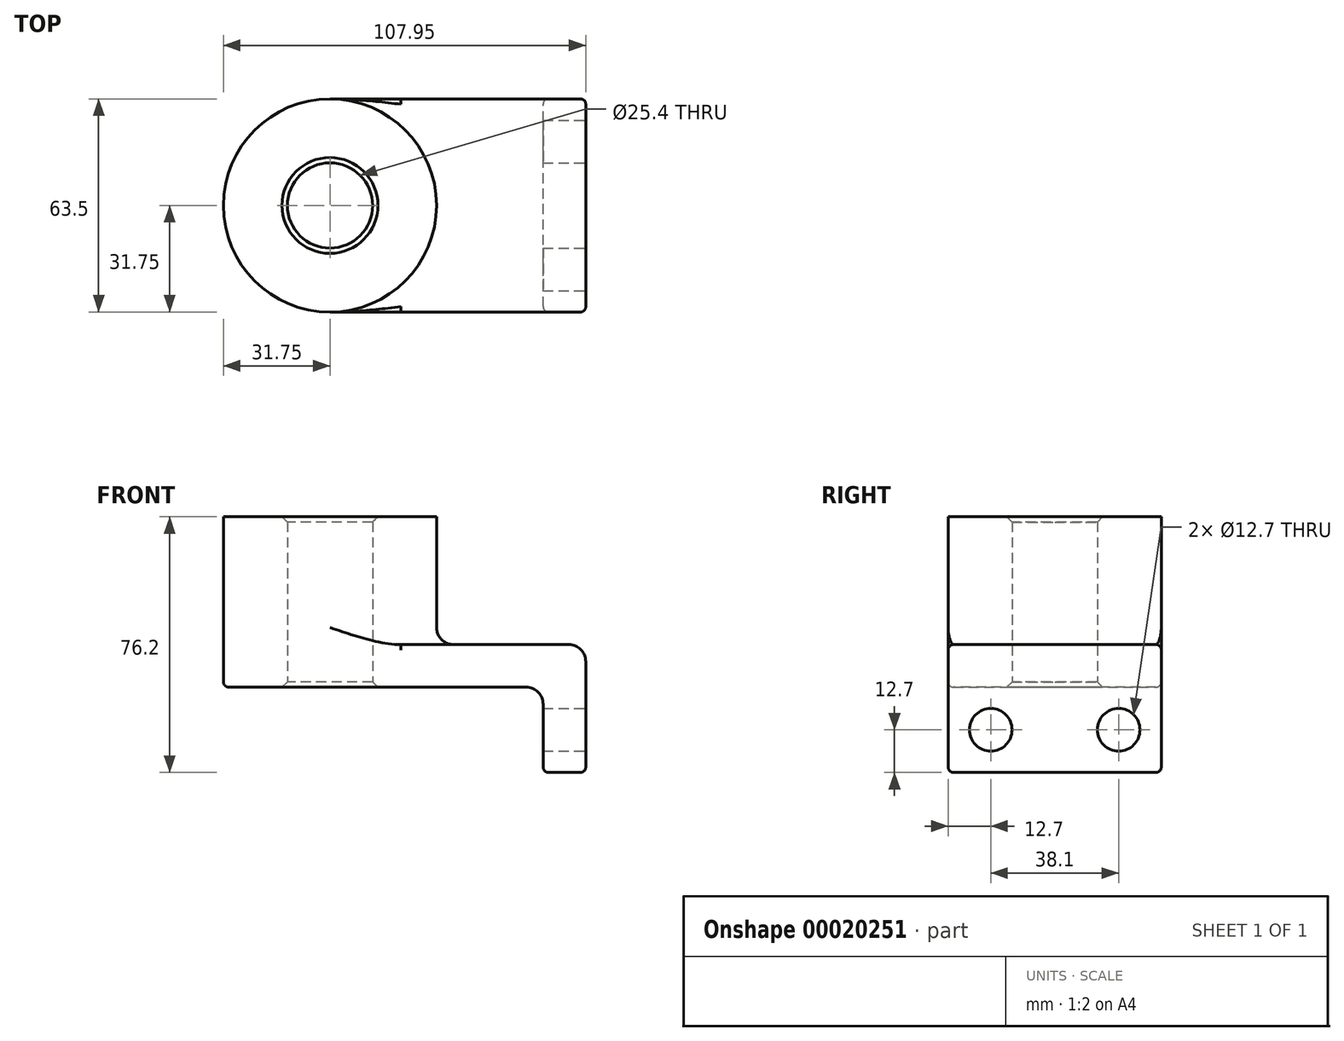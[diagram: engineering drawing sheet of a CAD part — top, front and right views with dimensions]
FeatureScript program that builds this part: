
annotation { "Feature Type Name" : "Feature", "Feature Type Description" : "" }
export const myFeature = defineFeature(function(context is Context, id is Id, definition is map)
    precondition{}
    {
        {
            var Q0;
            Q0=qCreatedBy(makeId("Top.planeOp"),FACE);
            var sketch = newSketch(context, id + "F0", { "sketchPlane" : qUnion([Q0])});
            skLineSegment(sketch, "E0.rect.bottom", {"start": v(-38.1, 31.75) * mm, "end": v(38.1, 31.75) * mm});
            skLineSegment(sketch, "E0.rect.top", {"start": v(-38.1, -31.75) * mm, "end": v(38.1, -31.75) * mm});
            skLineSegment(sketch, "E0.rect.left", {"start": v(-38.1, 31.75) * mm, "end": v(-38.1, -31.75) * mm});
            skLineSegment(sketch, "E0.rect.right", {"start": v(38.1, 31.75) * mm, "end": v(38.1, -31.75) * mm});
            skPoint(sketch, "E0.rect.middle", {"position": v(0, 0) * mm});
            skCircle(sketch, "E1", {"center": v(-38.1, 0) * mm, "radius": 31.75 * mm});
            skCircle(sketch, "E2", {"center": v(-38.1, 0) * mm, "radius": 12.7 * mm});
            skSolve(sketch);
        }
        {
            var Q0;
            Q0=qSketchRegion(id+"F0",true);
            extrude(context, id + "F1", {"entities" : qUnion([Q0]), "depth" : 12.7 * mm});
        }
        {
            var Q0;
            {var subQ0=sQuery(id+"F0.wireOp",EDGE,"E2");var subQ1=sQuery(id+"F0.wireOp",EDGE,"E0.rect.left");var subQ3=makeQuery(id+"F0.imprint","INTERSECT",VERTEX,{"disambiguationData":[OD(0.0)],"derivedFrom":[subQ1,subQ0]});Q0=makeQuery(id+"F0.imprint","IMPRINT",FACE,{"disambiguationData":[TD([[makeQuery(id+"F0.imprint","IMPRINT",EDGE,{"disambiguationData":[TD([[subQ3,-1.0]])],"derivedFrom":subQ0}),-1.0]])]});}
            var Q1;
            {var subQ0=sQuery(id+"F0.wireOp",EDGE,"E2");var subQ1=sQuery(id+"F0.wireOp",EDGE,"E0.rect.left");var subQ3=makeQuery(id+"F0.imprint","INTERSECT",VERTEX,{"disambiguationData":[OD(0.0)],"derivedFrom":[subQ1,subQ0]});Q1=makeQuery(id+"F0.imprint","IMPRINT",FACE,{"disambiguationData":[TD([[makeQuery(id+"F0.imprint","IMPRINT",EDGE,{"disambiguationData":[TD([[subQ3,1.0]])],"derivedFrom":subQ0}),-1.0]])]});}
            extrude(context, id + "F2", {"entities" : qUnion([Q0, Q1]), "operationType" : NewBodyOperationType.ADD, "depth" : 50.8 * mm});
        }
        {
            var Q0;
            Q0=makeQuery(id+"F1.opExtrude","SWEPT_FACE",FACE,{"disambiguationData":[OSD([sQuery(id+"F0.wireOp",EDGE,"E0.rect.right")])]});
            var sketch = newSketch(context, id + "F3", { "sketchPlane" : qUnion([Q0])});
            skLineSegment(sketch, "E3.bottom", {"start": v(-31.75, 12.7) * mm, "end": v(31.75, 12.7) * mm});
            skLineSegment(sketch, "E3.top", {"start": v(-31.75, -25.4) * mm, "end": v(31.75, -25.4) * mm});
            skLineSegment(sketch, "E3.left", {"start": v(-31.75, 12.7) * mm, "end": v(-31.75, -25.4) * mm});
            skLineSegment(sketch, "E3.right", {"start": v(31.75, 12.7) * mm, "end": v(31.75, -25.4) * mm});
            skCircle(sketch, "E4", {"center": v(-19.05, -12.7) * mm, "radius": 6.35 * mm});
            skLineSegment(sketch, "E5", {"start": v(0, 0) * mm, "end": v(0, -25.4) * mm, "construction": true});
            skCircle(sketch, "E6.0.MirrorC", {"center": v(19.05, -12.7) * mm, "radius": 6.35 * mm});
            skSolve(sketch);
        }
        {
            var Q0;
            Q0=qSketchRegion(id+"F3",true);
            extrude(context, id + "F4", {"entities" : qUnion([Q0]), "operationType" : NewBodyOperationType.ADD, "oppositeDirection" : true, "depth" : 12.7 * mm});
        }
        {
            var Q0;
            {var subQ0=sQuery(id+"F0.wireOp",EDGE,"E1");Q0=makeQuery(id+"F2.boolean.opBoolean","INTERSECT",EDGE,{"derivedFrom":[makeQuery(id+"F1.opExtrude","CAP_FACE",FACE,{"disambiguationData":[OSD([sQuery(id+"F0.wireOp",EDGE,"E0.rect.bottom"),sQuery(id+"F0.wireOp",EDGE,"E0.rect.top"),sQuery(id+"F0.wireOp",EDGE,"E0.rect.right"),subQ0,sQuery(id+"F0.wireOp",EDGE,"E2")])],"isStart":false}),makeQuery(id+"F2.opExtrude","SWEPT_FACE",FACE,{"disambiguationData":[OSD([subQ0])]})]});}
            var Q1;
            Q1=makeQuery(id+"F1.opExtrude","CAP_EDGE",EDGE,{"disambiguationData":[OSD([sQuery(id+"F0.wireOp",EDGE,"E0.rect.right")])],"isStart":false});
            var Q2;
            Q2=makeQuery(id+"F4.boolean.opBoolean","INTERSECT",EDGE,{"derivedFrom":[makeQuery(id+"F1.opExtrude","CAP_FACE",FACE,{"disambiguationData":[OSD([sQuery(id+"F0.wireOp",EDGE,"E0.rect.bottom"),sQuery(id+"F0.wireOp",EDGE,"E0.rect.top"),sQuery(id+"F0.wireOp",EDGE,"E0.rect.right"),sQuery(id+"F0.wireOp",EDGE,"E1"),sQuery(id+"F0.wireOp",EDGE,"E2")])],"isStart":true}),makeQuery(id+"F4.opExtrude","CAP_FACE",FACE,{"disambiguationData":[OSD([sQuery(id+"F3.wireOp",EDGE,"E3.bottom"),sQuery(id+"F3.wireOp",EDGE,"E3.top"),sQuery(id+"F3.wireOp",EDGE,"E3.left"),sQuery(id+"F3.wireOp",EDGE,"E3.right"),sQuery(id+"F3.wireOp",EDGE,"E4"),sQuery(id+"F3.wireOp",EDGE,"E6.0.MirrorC")])],"isStart":false})]});
            fillet(context, id + "F5", {"entities" : qUnion([Q0, Q1, Q2]), "radius" : 5.08 * mm, "tangentPropagation" : true, "allowEdgeOverflow" : false});
        }
        {
            var Q0;
            Q0=makeQuery(id+"F1.opExtrude","CAP_EDGE",EDGE,{"disambiguationData":[OSD([sQuery(id+"F0.wireOp",EDGE,"E0.rect.top")])],"isStart":false});
            var Q1;
            Q1=makeQuery(id+"F1.opExtrude","CAP_EDGE",EDGE,{"disambiguationData":[OSD([sQuery(id+"F0.wireOp",EDGE,"E0.rect.top")])],"isStart":true});
            var Q2;
            Q2=makeQuery(id+"F4.opExtrude","CAP_EDGE",EDGE,{"disambiguationData":[OSD([sQuery(id+"F3.wireOp",EDGE,"E3.left")])],"isStart":false});
            var Q3;
            Q3=makeQuery(id+"F4.boolean.opBoolean","MERGE",EDGE,{"derivedFrom":[makeQuery(id+"F1.opExtrude","SWEPT_EDGE",EDGE,{"disambiguationData":[OSD([sQuery(id+"F0.wireOp",EDGE,"E0.rect.top"),sQuery(id+"F0.wireOp",EDGE,"E0.rect.right")])]}),makeQuery(id+"F4.opExtrude","CAP_EDGE",EDGE,{"disambiguationData":[OSD([sQuery(id+"F3.wireOp",EDGE,"E3.left")])],"isStart":true})]});
            var Q4;
            Q4=makeQuery(id+"F4.opExtrude","CAP_EDGE",EDGE,{"disambiguationData":[OSD([sQuery(id+"F3.wireOp",EDGE,"E3.top")])],"isStart":true});
            var Q5;
            Q5=makeQuery(id+"F4.opExtrude","SWEPT_EDGE",EDGE,{"disambiguationData":[OSD([sQuery(id+"F3.wireOp",EDGE,"E3.top"),sQuery(id+"F3.wireOp",EDGE,"E3.left")])]});
            var Q6;
            Q6=makeQuery(id+"F4.opExtrude","SWEPT_EDGE",EDGE,{"disambiguationData":[OSD([sQuery(id+"F3.wireOp",EDGE,"E3.top"),sQuery(id+"F3.wireOp",EDGE,"E3.right")])]});
            var Q7;
            Q7=makeQuery(id+"F4.boolean.opBoolean","MERGE",EDGE,{"derivedFrom":[makeQuery(id+"F1.opExtrude","SWEPT_EDGE",EDGE,{"disambiguationData":[OSD([sQuery(id+"F0.wireOp",EDGE,"E0.rect.bottom"),sQuery(id+"F0.wireOp",EDGE,"E0.rect.right")])]}),makeQuery(id+"F4.opExtrude","CAP_EDGE",EDGE,{"disambiguationData":[OSD([sQuery(id+"F3.wireOp",EDGE,"E3.right")])],"isStart":true})]});
            var Q8;
            Q8=makeQuery(id+"F4.opExtrude","CAP_EDGE",EDGE,{"disambiguationData":[OSD([sQuery(id+"F3.wireOp",EDGE,"E3.right")])],"isStart":false});
            var Q9;
            Q9=makeQuery(id+"F4.opExtrude","CAP_EDGE",EDGE,{"disambiguationData":[OSD([sQuery(id+"F3.wireOp",EDGE,"E3.top")])],"isStart":false});
            var Q10;
            Q10=makeQuery(id+"F1.opExtrude","CAP_EDGE",EDGE,{"disambiguationData":[OSD([sQuery(id+"F0.wireOp",EDGE,"E0.rect.bottom")])],"isStart":false});
            fillet(context, id + "F6", {"entities" : qUnion([Q0, Q1, Q2, Q3, Q4, Q5, Q6, Q7, Q8, Q9, Q10]), "radius" : 1.59 * mm, "tangentPropagation" : true, "allowEdgeOverflow" : false});
        }
        {
            var Q0;
            {var subQ0=sQuery(id+"F0.wireOp",EDGE,"E2");Q0=makeQuery(id+"F2.boolean.opBoolean","MERGE",FACE,{"derivedFrom":[makeQuery(id+"F1.opExtrude","SWEPT_FACE",FACE,{"disambiguationData":[OSD([subQ0])]}),makeQuery(id+"F2.opExtrude","SWEPT_FACE",FACE,{"disambiguationData":[OSD([subQ0])]})]});}
            chamfer(context, id + "F7", {"entities" : qUnion([Q0]), "width" : 1.59 * mm, "tangentPropagation" : true});
        }
    });
